# Revit family: 355mm Roof Terminals BIM File
name_source: partatom
category: Air Terminals
units: mm (PartAtom-declared; Revit-internal decimal feet)

## family parameters
Always vertical = Yes
Cut with Voids When Loaded = No
Maintain Annotation Orientation = No
Part Type = Normal
Room Calculation Point = No
Round Connector Dimension = Use Diameter
Shared = No
Work Plane-Based = No

## types (2) — shared parameters
Cap dimensions (mm) = 550x660
Cap height (mm) = 160
Connection diameter = 355 mm  [stored 1.1647 ft]
Extract air flow at 20 Pa (m3/h) = 2600
Flow rate = 472.2 L/s
Installation instructions URL link = https://www.airflow.com
Lead dimensions (mm) = 900x750
Manufacturer = Airflow
Manufacturer's URL link = http://www.airflow.com
Manufacturer's name = Airflow
Material 1 = ANJ010016 1
Material 2 = ANJ010016 2
Material 4 = ANJ010016 4
Pressure = 100.0 Pa
Product URL link = https://www.airflow.com
Roof height (mm) = 215
Supply air flow at 20 Pa (m3/h) = 1700
URL = http://www.airflow.com
zero-valued in all types: Default Elevation

## per-type parameters (varying)
| type | Material 3 | Model | Part number | Product name |
| 355mm Terracotta Roof Terminal | ANJ010016 3 | 355mm Terracotta Roof Terminal | 90001408 | 355mm Terracotta Roof Terminal |
| 355mm dia Slate Roof Terminal | ANJ010016 3' | 355mm Slate Roof Terminal | 90001407 | 355mm Slate Roof Terminal |

note: [stored X ft] marks values corroborated as IEEE doubles in the binary element streams (Revit-internal decimal feet)

## geometry (parser evidence)
native form markers: Sweep x6
no freeform markers — native parametric forms only
